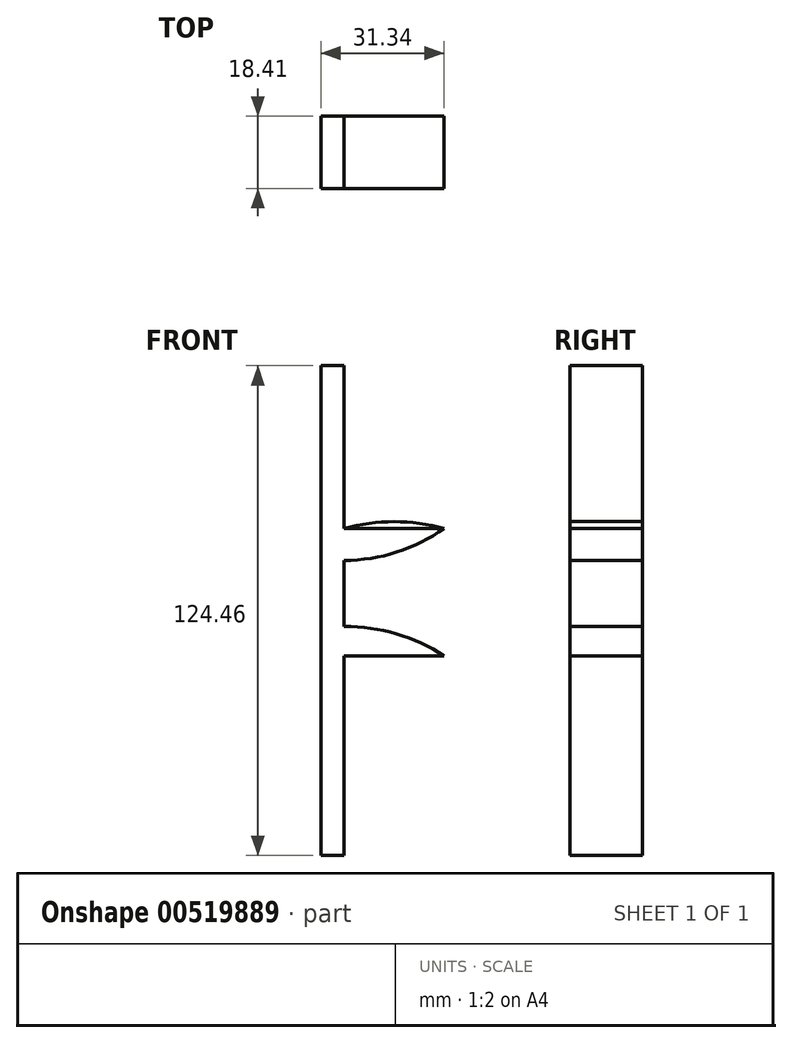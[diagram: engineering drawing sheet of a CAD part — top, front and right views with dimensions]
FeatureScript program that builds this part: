
annotation { "Feature Type Name" : "Feature", "Feature Type Description" : "" }
export const myFeature = defineFeature(function(context is Context, id is Id, definition is map)
    precondition{}
    {
        {
            var Q0;
            Q0=qCreatedBy(makeId("Right.planeOp"),FACE);
            var sketch = newSketch(context, id + "F0", { "sketchPlane" : qUnion([Q0])});
            skLineSegment(sketch, "E0.bottom", {"start": v(-11.4, 57.56) * mm, "end": v(7.01, 57.56) * mm});
            skLineSegment(sketch, "E0.top", {"start": v(-11.4, -66.9) * mm, "end": v(7.01, -66.9) * mm});
            skLineSegment(sketch, "E0.left", {"start": v(-11.4, 57.56) * mm, "end": v(-11.4, -66.9) * mm});
            skLineSegment(sketch, "E0.right", {"start": v(7.01, 57.56) * mm, "end": v(7.01, -66.9) * mm});
            skSolve(sketch);
        }
        {
            var Q0;
            Q0=makeQuery(id+"F0.imprint","IMPRINT",FACE,{"disambiguationData":[TD([[makeQuery(id+"F0.imprint","IMPRINT",EDGE,{"derivedFrom":sQuery(id+"F0.wireOp",EDGE,"E0.bottom")}),-1.0]])]});
            extrude(context, id + "F1", {"entities" : qUnion([Q0]), "depth" : 5.94 * mm, "offsetDistance" : 25.4 * mm});
        }
        {
            var Q0;
            Q0=makeQuery(id+"F1.opExtrude","CAP_FACE",FACE,{"disambiguationData":[OSD([sQuery(id+"F0.wireOp",EDGE,"E0.bottom"),sQuery(id+"F0.wireOp",EDGE,"E0.top"),sQuery(id+"F0.wireOp",EDGE,"E0.left"),sQuery(id+"F0.wireOp",EDGE,"E0.right")])],"isStart":false});
            var sketch = newSketch(context, id + "F2", { "sketchPlane" : qUnion([Q0])});
            skLineSegment(sketch, "E1", {"start": v(0, 0) * mm, "end": v(0, 16.2) * mm, "construction": true});
            skLineSegment(sketch, "E2", {"start": v(0, 16.2) * mm, "end": v(0, -16.2) * mm, "construction": true});
            skPoint(sketch, "E2.endSnap0", {"position": v(0, 8.1) * mm});
            skLineSegment(sketch, "E3", {"start": v(0, 16.2) * mm, "end": v(-11.4, 16.2) * mm});
            skLineSegment(sketch, "E4", {"start": v(-11.4, 16.2) * mm, "end": v(7.01, 16.2) * mm});
            skLineSegment(sketch, "E5", {"start": v(0, -16.2) * mm, "end": v(-11.4, -16.2) * mm});
            skLineSegment(sketch, "E6", {"start": v(-11.4, -16.2) * mm, "end": v(7.01, -16.2) * mm});
            skLineSegment(sketch, "E7", {"start": v(-11.4, 16.2) * mm, "end": v(-11.4, 8.08) * mm});
            skLineSegment(sketch, "E8", {"start": v(-11.4, 8.08) * mm, "end": v(7.01, 8.08) * mm});
            skLineSegment(sketch, "E9", {"start": v(-11.4, -16.2) * mm, "end": v(-11.4, -8.69) * mm});
            skLineSegment(sketch, "E10", {"start": v(-11.4, -8.69) * mm, "end": v(7.01, -8.69) * mm});
            skLineSegment(sketch, "E11", {"start": v(7.01, -8.69) * mm, "end": v(7.01, -16.2) * mm});
            skSolve(sketch);
        }
        {
            var Q0;
            Q0 = qSketchRegion(id + "F2", true);
            var Q1;
            {var subQ0=sQuery(id+"F2.wireOp",EDGE,"E7");Q1=makeQuery(id+"F2.imprint","IMPRINT",FACE,{"disambiguationData":[TD([[makeQuery(id+"F2.imprint","IMPRINT",EDGE,{"derivedFrom":subQ0}),1.0]])]});}
            extrude(context, id + "F3", {"entities" : qUnion([Q0, Q1]), "operationType" : NewBodyOperationType.ADD, "depth" : 25.4 * mm, "offsetDistance" : 25.4 * mm});
        }
        {
            var Q0;
            Q0 = qSketchRegion(id + "F2", true);
            extrude(context, id + "F4", {"entities" : qUnion([Q0]), "operationType" : NewBodyOperationType.ADD, "depth" : 25.4 * mm, "offsetDistance" : 25.4 * mm});
        }
        {
            var Q0;
            Q0=makeQuery(id+"F3.boolean.opBoolean","MERGE",FACE,{"derivedFrom":[makeQuery(id+"F1.opExtrude","SWEPT_FACE",FACE,{"disambiguationData":[OSD([sQuery(id+"F0.wireOp",EDGE,"E0.left")])]}),makeQuery(id+"F3.opExtrude","SWEPT_FACE",FACE,{"disambiguationData":[OSD([sQuery(id+"F2.wireOp",EDGE,"E7")])]}),makeQuery(id+"F3.opExtrude","SWEPT_FACE",FACE,{"disambiguationData":[OSD([sQuery(id+"F2.wireOp",EDGE,"E9")])]})]});
            var sketch = newSketch(context, id + "F5", { "sketchPlane" : qUnion([Q0])});
            skArc(sketch, "E12", {"start": v(5.94, 8.08) * mm, "mid": v(19.28, 10.16) * mm, "end": v(31.34, 16.2) * mm});
            skArc(sketch, "E13", {"start": v(31.34, -16.2) * mm, "mid": v(19.19, -10.6) * mm, "end": v(5.94, -8.69) * mm});
            skArc(sketch, "E14", {"start": v(5.94, -16.2) * mm, "mid": v(18.64, -17.91) * mm, "end": v(31.34, -16.2) * mm});
            skArc(sketch, "E15", {"start": v(31.34, 16.2) * mm, "mid": v(18.64, 17.91) * mm, "end": v(5.94, 16.2) * mm});
            skLineSegment(sketch, "E16", {"start": v(5.94, 16.2) * mm, "end": v(31.34, 16.2) * mm});
            skLineSegment(sketch, "E17", {"start": v(5.94, -16.2) * mm, "end": v(31.34, -16.2) * mm});
            skSolve(sketch);
        }
        {
            var Q0;
            Q0 = qSketchRegion(id + "F5", true);
            var Q1;
            Q1=makeQuery(id+"F5.imprint","IMPRINT",FACE,{"disambiguationData":[TD([[makeQuery(id+"F5.imprint","IMPRINT",EDGE,{"derivedFrom":sQuery(id+"F5.wireOp",EDGE,"E13")}),-1.0]])]});
            var Q2;
            Q2=makeQuery(id+"F5.imprint","IMPRINT",FACE,{"disambiguationData":[TD([[makeQuery(id+"F5.imprint","IMPRINT",EDGE,{"derivedFrom":sQuery(id+"F5.wireOp",EDGE,"E12")}),-1.0]])]});
            extrude(context, id + "F6", {"entities" : qUnion([Q0, Q1, Q2]), "operationType" : NewBodyOperationType.REMOVE, "oppositeDirection" : true, "depth" : 50.8 * mm, "offsetDistance" : 25.4 * mm});
        }
        {
            var Q0;
            Q0=makeQuery(id+"F5.imprint","IMPRINT",FACE,{"disambiguationData":[TD([[makeQuery(id+"F5.imprint","IMPRINT",EDGE,{"derivedFrom":sQuery(id+"F5.wireOp",EDGE,"E15")}),1.0]])]});
            extrude(context, id + "F7", {"entities" : qUnion([Q0]), "depth" : -18.41 * mm, "offsetDistance" : 25.4 * mm});
        }
    });
